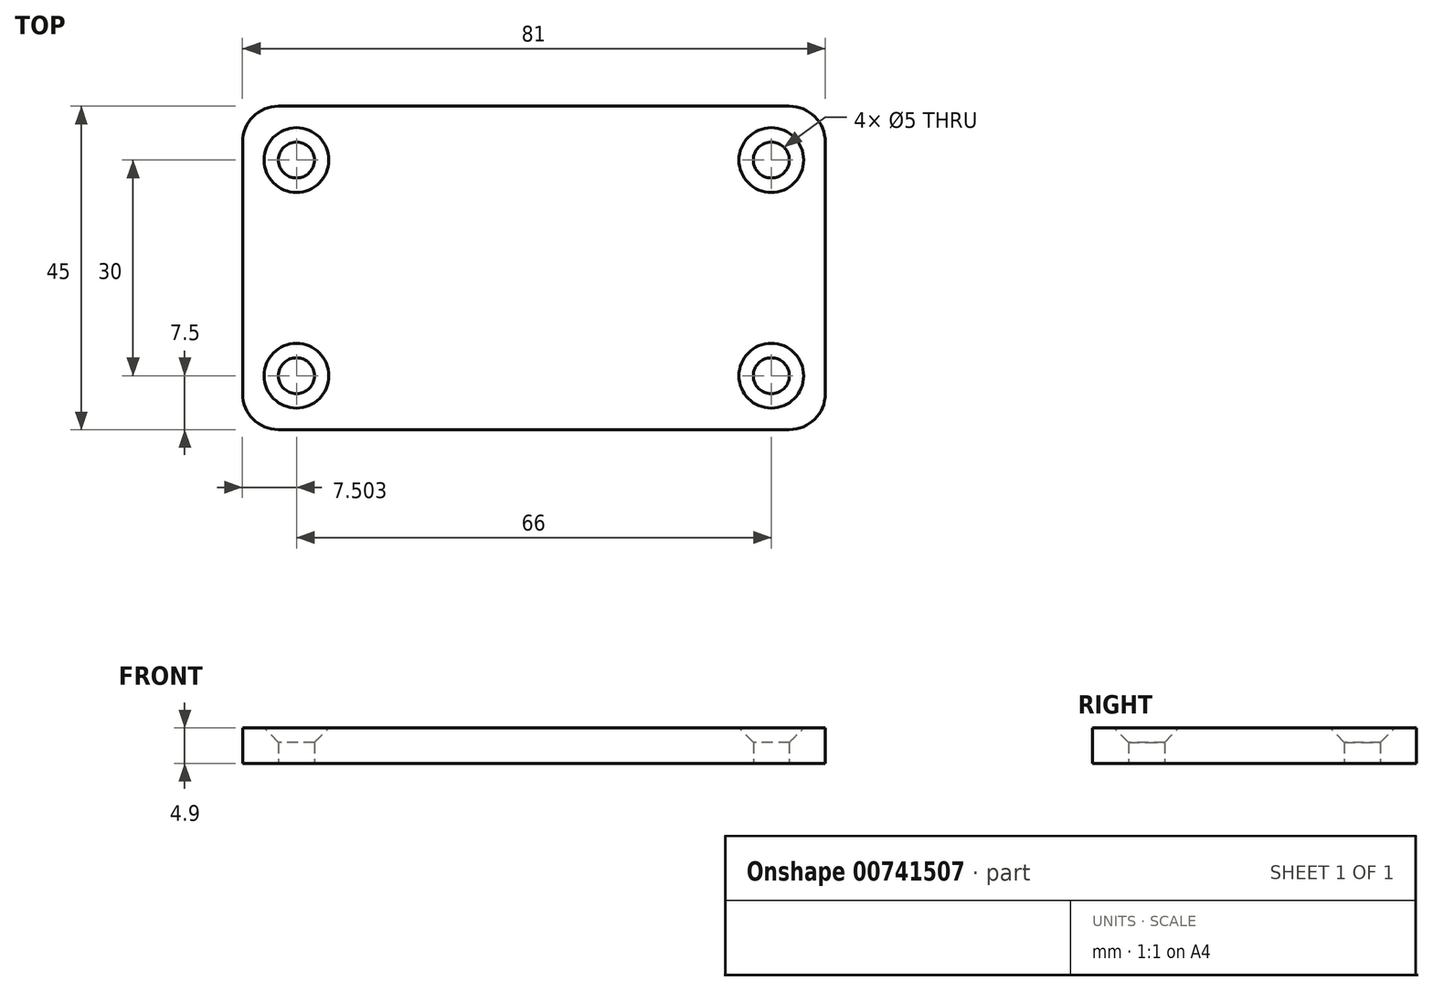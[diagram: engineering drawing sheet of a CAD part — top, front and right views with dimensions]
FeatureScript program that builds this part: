
annotation { "Feature Type Name" : "Feature", "Feature Type Description" : "" }
export const myFeature = defineFeature(function(context is Context, id is Id, definition is map)
    precondition{}
    {
        {
            var Q0;
            Q0=qCreatedBy(makeId("Top.planeOp"),FACE);
            var sketch = newSketch(context, id + "F0", { "sketchPlane" : qUnion([Q0])});
            skLineSegment(sketch, "E0.bottom", {"start": v(42.5, 7.5) * mm, "end": v(-38.5, 7.5) * mm});
            skLineSegment(sketch, "E0.top", {"start": v(42.5, -7.5) * mm, "end": v(-38.5, -7.5) * mm});
            skLineSegment(sketch, "E0.left", {"start": v(42.5, 7.5) * mm, "end": v(42.5, -7.5) * mm});
            skLineSegment(sketch, "E0.right", {"start": v(-38.5, 7.5) * mm, "end": v(-38.5, -7.5) * mm});
            skPoint(sketch, "E0.middle", {"position": v(2, 0) * mm});
            skCircle(sketch, "E1", {"center": v(-31, 0) * mm, "radius": 2.5 * mm});
            skCircle(sketch, "E2", {"center": v(35, 0) * mm, "radius": 2.5 * mm});
            skLineSegment(sketch, "E3.bottom", {"start": v(-38.5, -7.5) * mm, "end": v(42.5, -7.5) * mm});
            skLineSegment(sketch, "E3.top", {"start": v(-38.5, -37.5) * mm, "end": v(42.5, -37.5) * mm});
            skLineSegment(sketch, "E3.left", {"start": v(-38.5, -7.5) * mm, "end": v(-38.5, -37.5) * mm});
            skLineSegment(sketch, "E3.right", {"start": v(42.5, -7.5) * mm, "end": v(42.5, -37.5) * mm});
            skCircle(sketch, "E4", {"center": v(-31, -30) * mm, "radius": 2.5 * mm});
            skCircle(sketch, "E5", {"center": v(35, -30) * mm, "radius": 2.5 * mm});
            skSolve(sketch);
        }
        {
            var Q0;
            Q0 = qSketchRegion(id + "F0", true);
            extrude(context, id + "F1", {"entities" : qUnion([Q0]), "depth" : 4.9 * mm, "offsetDistance" : 25 * mm});
        }
        {
            var Q0;
            Q0=makeQuery(id+"F1.opExtrude","SWEPT_EDGE",EDGE,{"disambiguationData":[OSD([sQuery(id+"F0.wireOp",EDGE,"E0.top"),sQuery(id+"F0.wireOp",EDGE,"E0.left")])]});
            var Q1;
            Q1=makeQuery(id+"F1.opExtrude","SWEPT_EDGE",EDGE,{"disambiguationData":[OSD([sQuery(id+"F0.wireOp",EDGE,"E0.bottom"),sQuery(id+"F0.wireOp",EDGE,"E0.left")])]});
            var Q2;
            Q2=makeQuery(id+"F1.opExtrude","SWEPT_EDGE",EDGE,{"disambiguationData":[OSD([sQuery(id+"F0.wireOp",EDGE,"E0.bottom"),sQuery(id+"F0.wireOp",EDGE,"E0.right")])]});
            var Q3;
            Q3=makeQuery(id+"F1.opExtrude","SWEPT_EDGE",EDGE,{"disambiguationData":[OSD([sQuery(id+"F0.wireOp",EDGE,"E0.top"),sQuery(id+"F0.wireOp",EDGE,"E0.right")])]});
            fillet(context, id + "F2", {"entities" : qUnion([Q0, Q1, Q2, Q3]), "radius" : 5 * mm, "tangentPropagation" : true, "allowEdgeOverflow" : false});
        }
        {
            var Q0;
            Q0=makeQuery(id+"F1.opExtrude","SWEPT_EDGE",EDGE,{"disambiguationData":[OSD([sQuery(id+"F0.wireOp",EDGE,"E3.top"),sQuery(id+"F0.wireOp",EDGE,"E3.right")])]});
            var Q1;
            Q1=makeQuery(id+"F1.opExtrude","SWEPT_EDGE",EDGE,{"disambiguationData":[OSD([sQuery(id+"F0.wireOp",EDGE,"E3.top"),sQuery(id+"F0.wireOp",EDGE,"E3.left")])]});
            fillet(context, id + "F3", {"entities" : qUnion([Q0, Q1]), "radius" : 5 * mm, "tangentPropagation" : true, "allowEdgeOverflow" : false});
        }
        {
            var Q0;
            Q0=makeQuery(id+"F1.opExtrude","CAP_EDGE",EDGE,{"disambiguationData":[OSD([sQuery(id+"F0.wireOp",EDGE,"E2")])],"isStart":false});
            var Q1;
            Q1=makeQuery(id+"F1.opExtrude","CAP_EDGE",EDGE,{"disambiguationData":[OSD([sQuery(id+"F0.wireOp",EDGE,"E5")])],"isStart":false});
            var Q2;
            Q2=makeQuery(id+"F1.opExtrude","CAP_EDGE",EDGE,{"disambiguationData":[OSD([sQuery(id+"F0.wireOp",EDGE,"E1")])],"isStart":false});
            var Q3;
            Q3=makeQuery(id+"F1.opExtrude","CAP_EDGE",EDGE,{"disambiguationData":[OSD([sQuery(id+"F0.wireOp",EDGE,"E4")])],"isStart":false});
            chamfer(context, id + "F4", {"entities" : qUnion([Q0, Q1, Q2, Q3]), "width" : 2 * mm, "tangentPropagation" : true});
        }
    });
